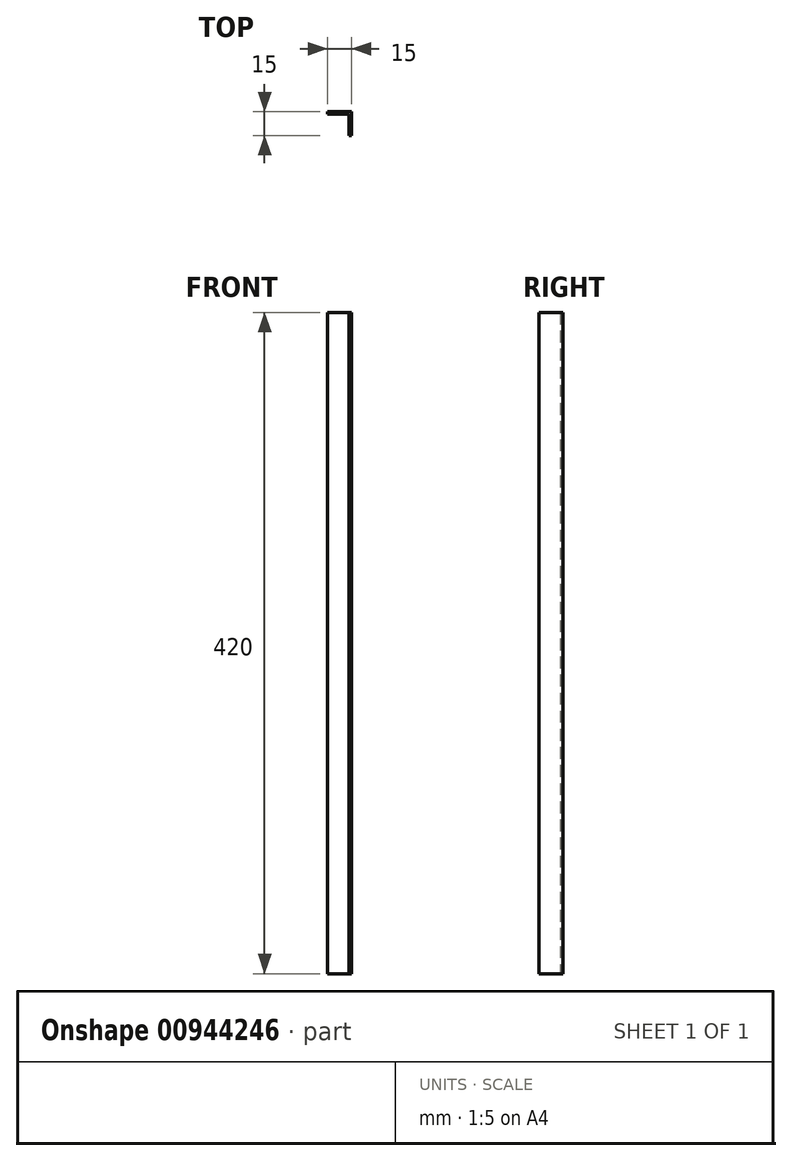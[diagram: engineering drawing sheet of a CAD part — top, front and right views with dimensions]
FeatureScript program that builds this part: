
annotation { "Feature Type Name" : "Feature", "Feature Type Description" : "" }
export const myFeature = defineFeature(function(context is Context, id is Id, definition is map)
    precondition{}
    {
        {
            var Q0;
            Q0=qCreatedBy(makeId("Top.planeOp"),FACE);
            var sketch = newSketch(context, id + "F0", { "sketchPlane" : qUnion([Q0])});
            skLineSegment(sketch, "E0.bottom", {"start": v(7.5, 7.5) * mm, "end": v(-7.5, 7.5) * mm});
            skLineSegment(sketch, "E0.left", {"start": v(7.5, 7.5) * mm, "end": v(7.5, -7.5) * mm});
            skPoint(sketch, "E0.middle", {"position": v(0, 0) * mm});
            skLineSegment(sketch, "E1", {"start": v(-7.5, 7.5) * mm, "end": v(-7.5, 6) * mm});
            skLineSegment(sketch, "E2", {"start": v(7.5, -7.5) * mm, "end": v(6, -7.5) * mm});
            skLineSegment(sketch, "E3", {"start": v(-7.5, 6) * mm, "end": v(6, 6) * mm});
            skLineSegment(sketch, "E4", {"start": v(6, 6) * mm, "end": v(6, -7.5) * mm});
            skSolve(sketch);
        }
        {
            var Q0;
            Q0=makeQuery(id+"F0.imprint","IMPRINT",FACE,{"disambiguationData":[TD([[makeQuery(id+"F0.imprint","IMPRINT",EDGE,{"derivedFrom":sQuery(id+"F0.wireOp",EDGE,"E0.bottom")}),1.0]])]});
            extrude(context, id + "F1", {"entities" : qUnion([Q0]), "depth" : 420 * mm, "offsetDistance" : 25 * mm});
        }
    });
